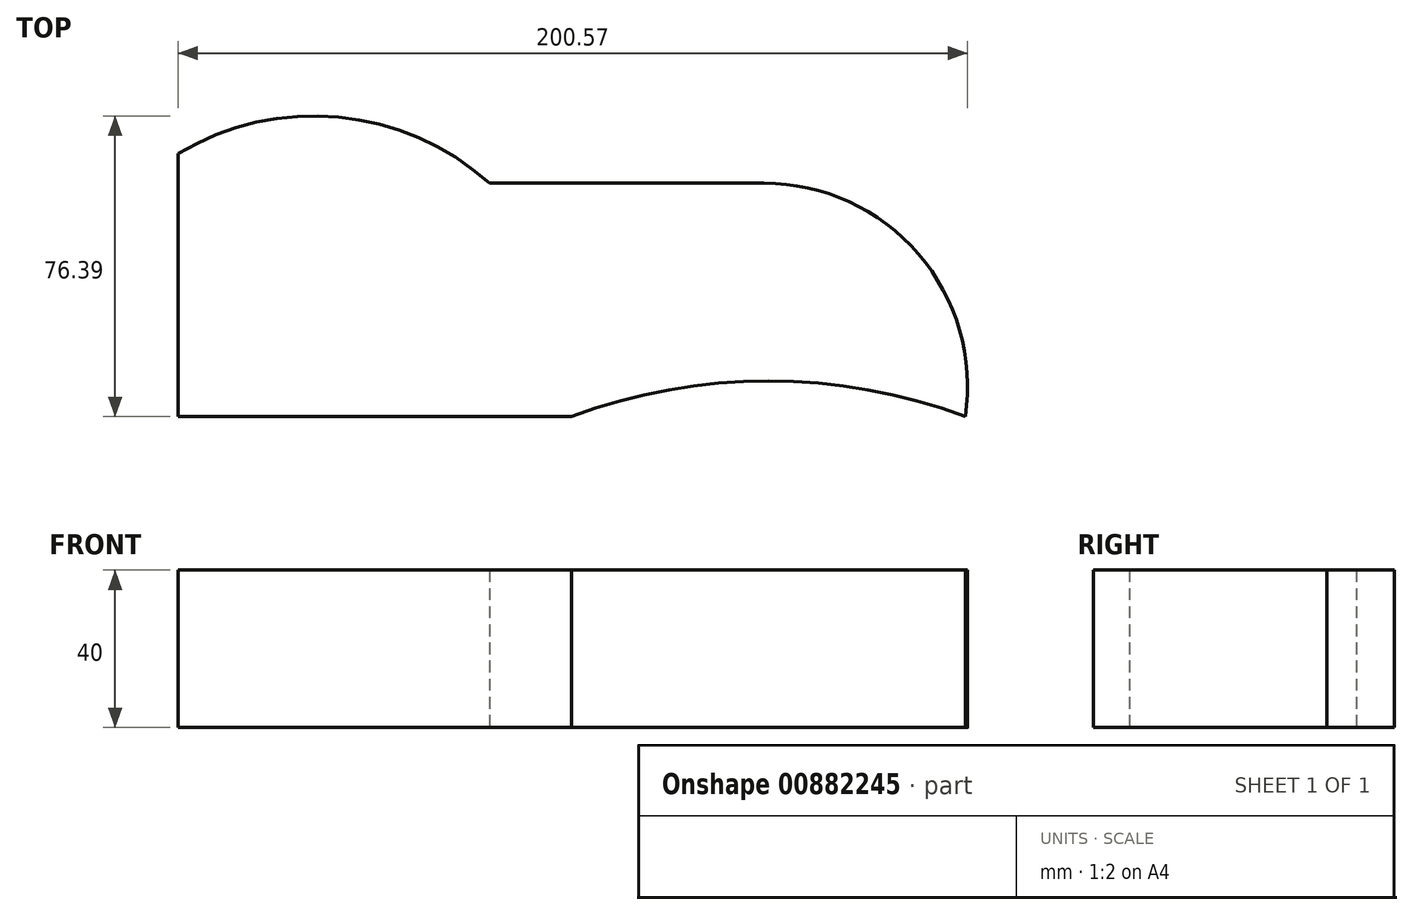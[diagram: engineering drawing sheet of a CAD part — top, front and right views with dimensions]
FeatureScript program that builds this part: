
annotation { "Feature Type Name" : "Feature", "Feature Type Description" : "" }
export const myFeature = defineFeature(function(context is Context, id is Id, definition is map)
    precondition{}
    {
        {
            var Q0;
            Q0=qCreatedBy(makeId("Top.planeOp"),FACE);
            var sketch = newSketch(context, id + "F0", { "sketchPlane" : qUnion([Q0])});
            skPoint(sketch, "E0.end.orphan", {"position": v(-34.9, 0) * mm});
            skPoint(sketch, "E1.start.orphan", {"position": v(-115.04, -24.97) * mm});
            skPoint(sketch, "E2.end.orphan", {"position": v(-15.04, -24.97) * mm});
            skPoint(sketch, "E2.start.orphan", {"position": v(84.96, -24.97) * mm});
            skLineSegment(sketch, "E3", {"start": v(-115.04, -24.97) * mm, "end": v(-115.04, 41.82) * mm});
            skLineSegment(sketch, "E4", {"start": v(-115.04, -24.97) * mm, "end": v(-15.04, -24.97) * mm});
            skArc(sketch, "E5", {"start": v(-35.96, 34.35) * mm, "mid": v(-74.27, 51.12) * mm, "end": v(-115.04, 41.82) * mm});
            skLineSegment(sketch, "E6", {"start": v(-35.96, 34.35) * mm, "end": v(33.88, 34.35) * mm});
            skArc(sketch, "E7", {"start": v(84.96, -24.97) * mm, "mid": v(73.02, 16.4) * mm, "end": v(33.88, 34.35) * mm});
            skArc(sketch, "E8", {"start": v(84.96, -24.97) * mm, "mid": v(34.96, -15.88) * mm, "end": v(-15.04, -24.97) * mm});
            skSolve(sketch);
        }
        {
            var Q0;
            Q0 = qSketchRegion(id + "F0", true);
            extrude(context, id + "F1", {"entities" : qUnion([Q0]), "depth" : 40 * mm, "offsetDistance" : 25 * mm});
        }
    });
